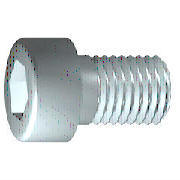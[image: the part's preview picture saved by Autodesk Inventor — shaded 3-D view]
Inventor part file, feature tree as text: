
AUTODESK INVENTOR PART (.ipt)
format: ipt  version: 2020 (Build 240168000, 168)  size: 191,488 bytes
history: native  units: mm (DEFAULTED — no unit token found)
features: sketch x2, extrude x1, plane x1, fillet x1
ambient origin geometry x7: Origin, YZ Plane, XY Plane, X Axis, Y Axis, Z Axis, Center Point
bodies: Solid1 (feature_tree), Body (feature_tree)
feature tree (5):
  extrude  "Slot"  Depth=3.0mm
  plane  "Work Plane1"
  fillet  "Fillet2"  Radius=3.0mm
  sketch  "Sketch1"  dims[d1=14.75mm d2=0.306825mm d3=3.0mm]
  sketch  "Sketch2"  dims[d4=1.3mm d5=60.0deg d6=3.0mm d7=3.0mm d8=2.886751mm d9=5.5mm d10=90.0deg d11=10.0mm d12=0.0mm d13=14.75mm d14=0.0mm d15=0.306725mm d16=0.306725mm d17=0.3mm d19=0.0mm d26=16.0mm d27=45.0deg d28=0.0mm d29=0.0mm d30=0.1mm]
